SOLIDWORKS PART (.sldprt)
format: sldprt  version: not decoded by parser v0  size: 235,520 bytes
history: native  units: mm
features: sketch x6, extrude x5, plane x3, chamfer x2, fillet x2, material x1, cut_extrude x1 (+10 scaffold rows collapsed)
feature tree (30):
  scaffold x10  (default folders/planes/origin — collapsed)
  material  "Matériau <non spécifié>"
  plane  "Plan de face"
  plane  "Plan de dessus"
  plane  "Plan de droite"
  sketch  "Esquisse1"  dims[D1=36.3mm D2=40.5mm D3=20.25mm D4=27.8mm D5=2.55mm D6=3.5mm D7=19.5mm D8=2.5mm D9=3.5mm D10=7.7mm]
  extrude  "Extrusion1"  Depth=19.5mm
  sketch  "Esquisse3"  dims[D5=~1.552422mm D1=20.25mm D2=9.75mm D3=4.0mm D4=4.0mm]
  cut_extrude  "Enlèv. mat.-Extru.1"  [1 undecoded]
  sketch  "Esquisse4"  dims[D3=~3.299983mm D1=9.75mm D2=9.75mm]
  extrude  "Extrusion2"  Depth=2mm
  sketch  "Esquisse5"  dims[D1=~0.976795mm]
  extrude  "Extrusion3"  Depth=3.5mm
  chamfer  "Chanfrein1"  Distance=2mm Angle=45deg
  sketch  "Esquisse6"  dims[D1=20.25mm D2=9.75mm D3=4.0mm D4=1.5mm D5=0.75mm]
  extrude  "Extrusion4"  Depth=2mm
  chamfer  "Chanfrein2"  Distance=1mm Angle=60deg
  sketch  "Esquisse8"  dims[D1=9.75mm D2=4.0mm D3=8.0mm D4=4.0mm D5=1.0mm D6=5.0mm D7=1.5mm D8=1.5mm]
  extrude  "Extrusion5"  Depth=2mm
  fillet  "Congé2"  Radius=0.5mm
  fillet  "Congé3"  Radius=0.3mm
decode coverage: 15 of 16 modeling features carry decoded parameters
note: ~ marks probable driven/reference dimensions
note: 1 parameter value undecoded
note: suppression state not decoded; provenance and decode notes live in map.json
